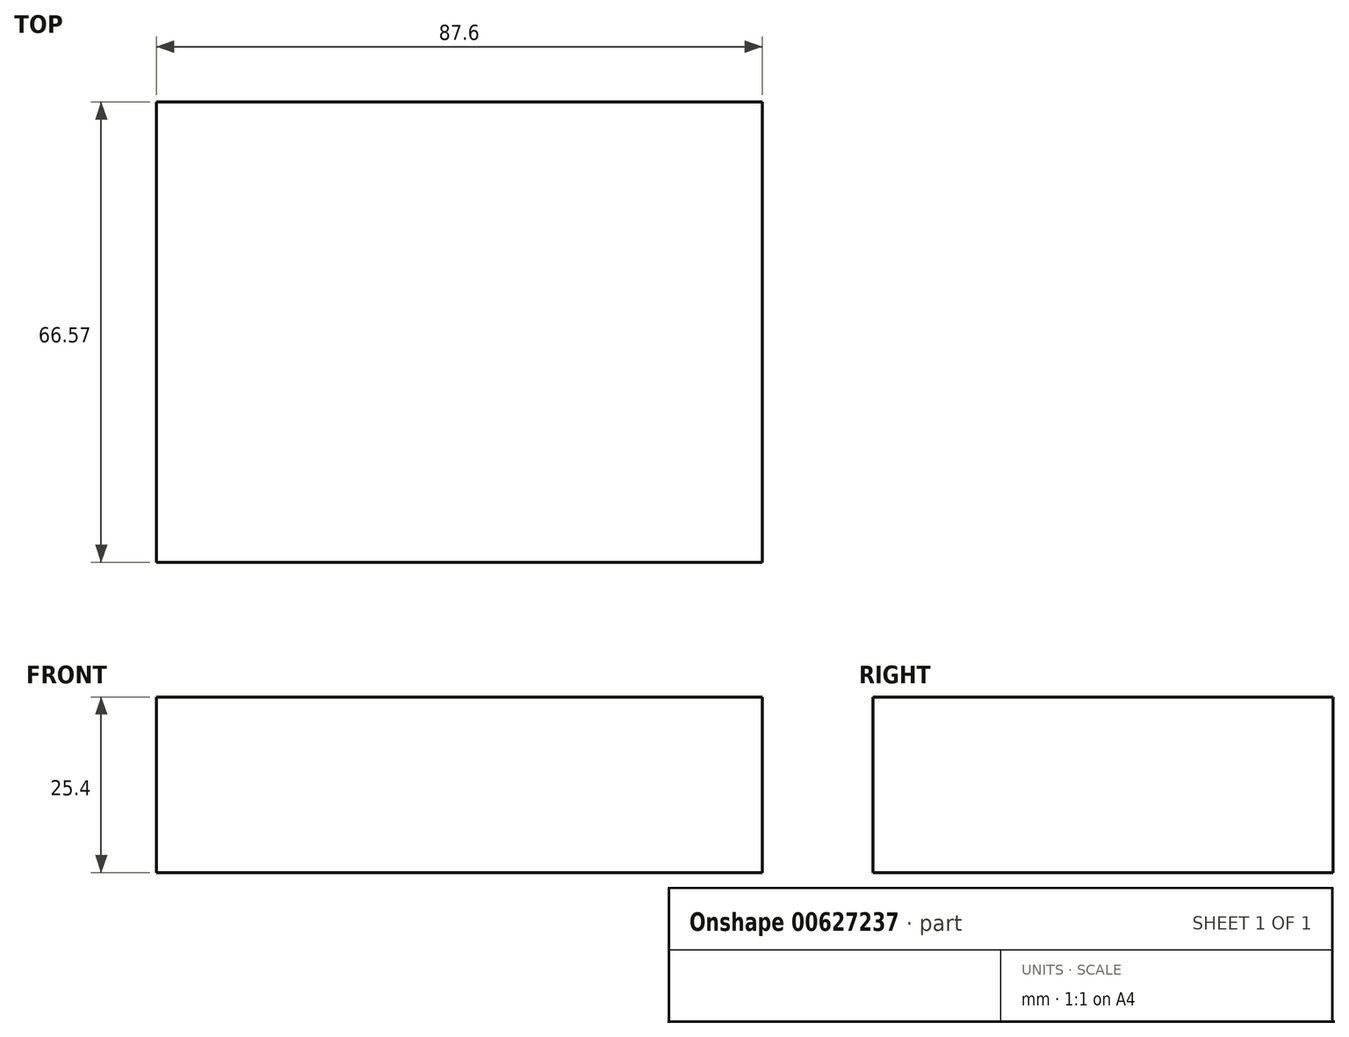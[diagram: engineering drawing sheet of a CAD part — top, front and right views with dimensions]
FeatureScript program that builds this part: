
annotation { "Feature Type Name" : "Feature", "Feature Type Description" : "" }
export const myFeature = defineFeature(function(context is Context, id is Id, definition is map)
    precondition{}
    {
        {
            var Q0;
            Q0=qCreatedBy(makeId("Top.planeOp"),FACE);
            var sketch = newSketch(context, id + "F0", { "sketchPlane" : qUnion([Q0])});
            skLineSegment(sketch, "E0.bottom", {"start": v(-57.09, 37.52) * mm, "end": v(30.51, 37.52) * mm});
            skLineSegment(sketch, "E0.top", {"start": v(-57.09, -29.05) * mm, "end": v(30.51, -29.05) * mm});
            skLineSegment(sketch, "E0.left", {"start": v(-57.09, 37.52) * mm, "end": v(-57.09, -29.05) * mm});
            skLineSegment(sketch, "E0.right", {"start": v(30.51, 37.52) * mm, "end": v(30.51, -29.05) * mm});
            skSolve(sketch);
        }
        {
            var Q0;
            Q0=makeQuery(id+"F0.imprint","IMPRINT",FACE,{"disambiguationData":[TD([[makeQuery(id+"F0.imprint","IMPRINT",EDGE,{"derivedFrom":sQuery(id+"F0.wireOp",EDGE,"E0.bottom")}),-1.0]])]});
            extrude(context, id + "F1", {"entities" : qUnion([Q0]), "depth" : 25.4 * mm, "offsetDistance" : 25.4 * mm});
        }
    });
